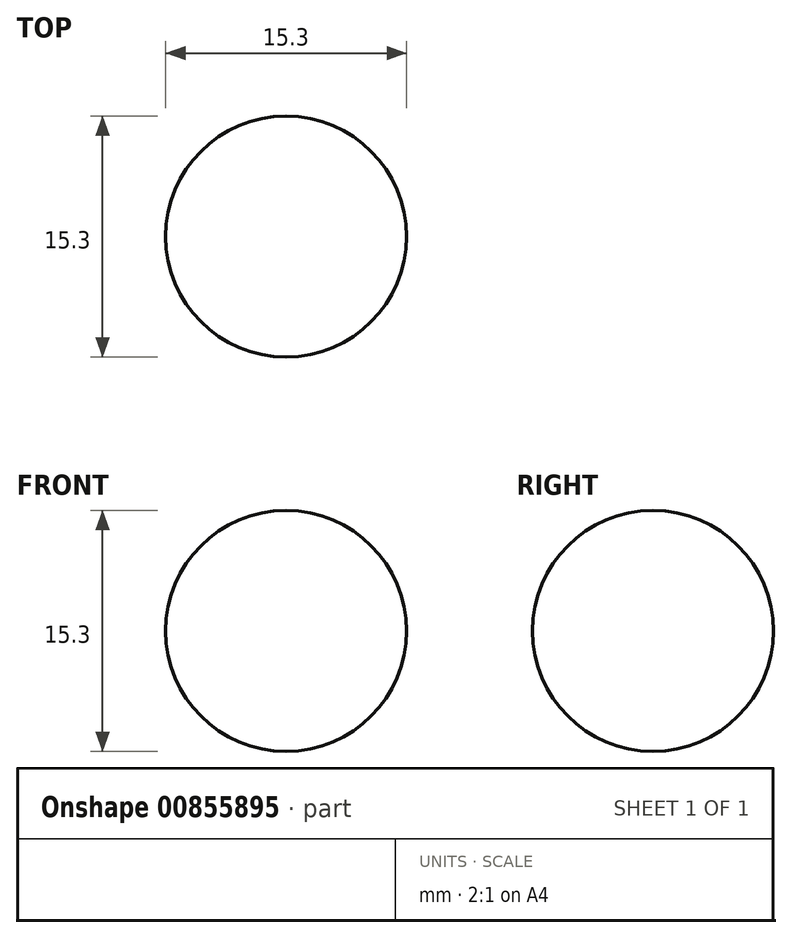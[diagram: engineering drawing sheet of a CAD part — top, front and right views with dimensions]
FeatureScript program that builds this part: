
annotation { "Feature Type Name" : "Feature", "Feature Type Description" : "" }
export const myFeature = defineFeature(function(context is Context, id is Id, definition is map)
    precondition{}
    {
        {
            var Q0;
            Q0=qCreatedBy(makeId("Front.planeOp"),FACE);
            var sketch = newSketch(context, id + "F0", { "sketchPlane" : qUnion([Q0])});
            skLineSegment(sketch, "E0", {"start": v(-7.65, 0) * mm, "end": v(7.65, 0) * mm});
            skArc(sketch, "E1", {"start": v(-7.65, 0) * mm, "mid": v(0, -7.65) * mm, "end": v(7.65, 0) * mm});
            skSolve(sketch);
        }
        {
            var Q0;
            Q0=qSketchRegion(id+"F0",true);
            var Q1;
            Q1=sQuery(id+"F0.wireOp",EDGE,"E0");
            revolve(context, id + "F1", {"surfaceOperationType" : NewSurfaceOperationType.NEW, "entities" : qUnion([Q0]), "axis" : qUnion([Q1]), "revolveType" : RevolveType.FULL});
        }
    });
